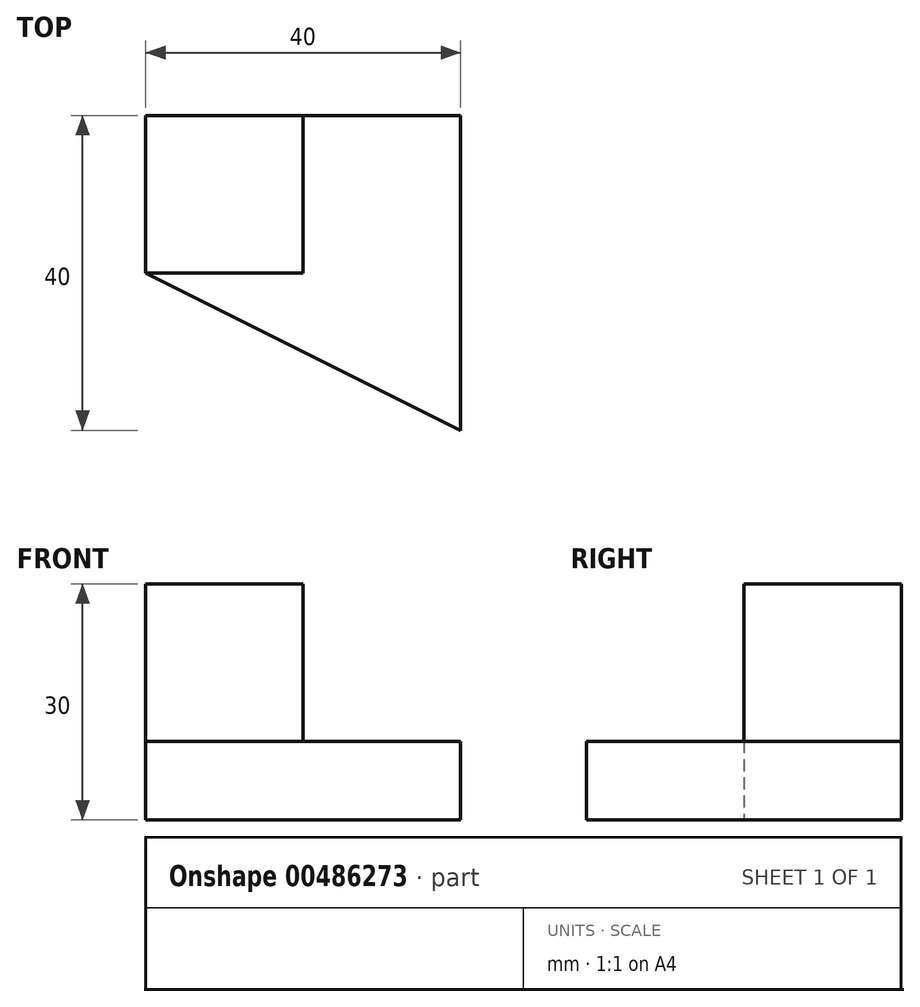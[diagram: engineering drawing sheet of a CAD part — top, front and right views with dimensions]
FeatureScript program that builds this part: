
annotation { "Feature Type Name" : "Feature", "Feature Type Description" : "" }
export const myFeature = defineFeature(function(context is Context, id is Id, definition is map)
    precondition{}
    {
        {
            var Q0;
            Q0=qCreatedBy(makeId("Front.planeOp"),FACE);
            var sketch = newSketch(context, id + "F0", { "sketchPlane" : qUnion([Q0])});
            skEllipse(sketch, "E0", {"center": v(-55.38, 51.75) * mm, "majorRadius": 36.82 * mm, "minorRadius": 23.2 * mm, "majorAxis": v(0.88, -0.47)});
            skSolve(sketch);
        }
        {
            var Q0;
            Q0 = qSketchRegion(id + "F0", true);
            extrude(context, id + "F1", {"entities" : qUnion([Q0]), "depth" : 0 * mm});
        }
        {
            var Q0;
            Q0=qCreatedBy(makeId("Right.planeOp"),FACE);
            var sketch = newSketch(context, id + "F2", { "sketchPlane" : qUnion([Q0])});
            skCircle(sketch, "E1.cCircle", {"center": v(-62.83, 49.28) * mm, "radius": 31.28 * mm, "construction": true});
            skLineSegment(sketch, "E1.0", {"start": v(-40.14, 27.75) * mm, "end": v(-70.13, 18.87) * mm});
            skLineSegment(sketch, "E1.1", {"start": v(-70.13, 18.87) * mm, "end": v(-92.82, 40.4) * mm});
            skLineSegment(sketch, "E1.2", {"start": v(-92.82, 40.4) * mm, "end": v(-85.52, 70.8) * mm});
            skLineSegment(sketch, "E1.3", {"start": v(-85.52, 70.8) * mm, "end": v(-55.53, 79.7) * mm});
            skLineSegment(sketch, "E1.4", {"start": v(-55.53, 79.7) * mm, "end": v(-32.85, 58.16) * mm});
            skLineSegment(sketch, "E1.5", {"start": v(-32.85, 58.16) * mm, "end": v(-40.14, 27.75) * mm});
            skSolve(sketch);
        }
        {
            var Q0;
            Q0 = qSketchRegion(id + "F2", true);
            extrude(context, id + "F3", {"entities" : qUnion([Q0]), "depth" : 457.2 * mm});
        }
        {
            var Q0;
            Q0=makeQuery(id+"F3.opExtrude","SWEPT_BODY",BODY,{"disambiguationData":[OSD([sQuery(id+"F2.wireOp",EDGE,"E1.0"),sQuery(id+"F2.wireOp",EDGE,"E1.1"),sQuery(id+"F2.wireOp",EDGE,"E1.2"),sQuery(id+"F2.wireOp",EDGE,"E1.3"),sQuery(id+"F2.wireOp",EDGE,"E1.4"),sQuery(id+"F2.wireOp",EDGE,"E1.5")])]});
            deleteBodies(context, id + "F4", {"entities" : qUnion([Q0])});
        }
        {
            var Q0;
            Q0=makeQuery(id+"F1.opExtrude","SWEPT_BODY",BODY,{"disambiguationData":[OSD([sQuery(id+"F0.wireOp",EDGE,"E0")])]});
            deleteBodies(context, id + "F5", {"entities" : qUnion([Q0])});
        }
        {
            var Q0;
            Q0=qCreatedBy(makeId("Top.planeOp"),FACE);
            var sketch = newSketch(context, id + "F6", { "sketchPlane" : qUnion([Q0])});
            skLineSegment(sketch, "E2", {"start": v(-28, 32.33) * mm, "end": v(-8, 32.33) * mm});
            skLineSegment(sketch, "E3", {"start": v(-8, 32.33) * mm, "end": v(-8, 12.33) * mm});
            skLineSegment(sketch, "E4", {"start": v(-8, 12.33) * mm, "end": v(-28, 12.33) * mm});
            skLineSegment(sketch, "E5", {"start": v(-28, 12.33) * mm, "end": v(-28, 32.33) * mm});
            skLineSegment(sketch, "E6", {"start": v(-8, 32.33) * mm, "end": v(12, 32.33) * mm});
            skLineSegment(sketch, "E7", {"start": v(12, 32.33) * mm, "end": v(12, -7.67) * mm});
            skLineSegment(sketch, "E8", {"start": v(12, -7.67) * mm, "end": v(-28, 12.33) * mm});
            skSolve(sketch);
        }
        {
            var Q0;
            Q0=makeQuery(id+"F6.imprint","IMPRINT",FACE,{"disambiguationData":[TD([[makeQuery(id+"F6.imprint","IMPRINT",EDGE,{"derivedFrom":sQuery(id+"F6.wireOp",EDGE,"E3")}),1.0]])]});
            var Q1;
            Q1=makeQuery(id+"F6.imprint","IMPRINT",FACE,{"disambiguationData":[TD([[makeQuery(id+"F6.imprint","IMPRINT",EDGE,{"derivedFrom":sQuery(id+"F6.wireOp",EDGE,"E2")}),-1.0]])]});
            extrude(context, id + "F7", {"entities" : qUnion([Q0, Q1]), "depth" : 10 * mm});
        }
        {
            var Q0;
            Q0=makeQuery(id+"F7.opExtrude","CAP_FACE",FACE,{"disambiguationData":[OSD([sQuery(id+"F6.wireOp",EDGE,"E2"),sQuery(id+"F6.wireOp",EDGE,"E5"),sQuery(id+"F6.wireOp",EDGE,"E6"),sQuery(id+"F6.wireOp",EDGE,"E7"),sQuery(id+"F6.wireOp",EDGE,"E8")])],"isStart":false});
            var sketch = newSketch(context, id + "F8", { "sketchPlane" : qUnion([Q0])});
            skLineSegment(sketch, "E9", {"start": v(-28, 32.33) * mm, "end": v(-8, 32.33) * mm});
            skLineSegment(sketch, "E10", {"start": v(-8, 32.33) * mm, "end": v(-8, 12.33) * mm});
            skLineSegment(sketch, "E11", {"start": v(-8, 12.33) * mm, "end": v(-28, 12.33) * mm});
            skLineSegment(sketch, "E12", {"start": v(-28, 12.33) * mm, "end": v(-28, 32.33) * mm});
            skSolve(sketch);
        }
        {
            var Q0;
            Q0=makeQuery(id+"F8.imprint","IMPRINT",FACE,{"disambiguationData":[TD([[makeQuery(id+"F8.imprint","IMPRINT",EDGE,{"derivedFrom":sQuery(id+"F8.wireOp",EDGE,"E9")}),-1.0]])]});
            extrude(context, id + "F9", {"entities" : qUnion([Q0]), "operationType" : NewBodyOperationType.ADD, "depth" : 20 * mm});
        }
    });
